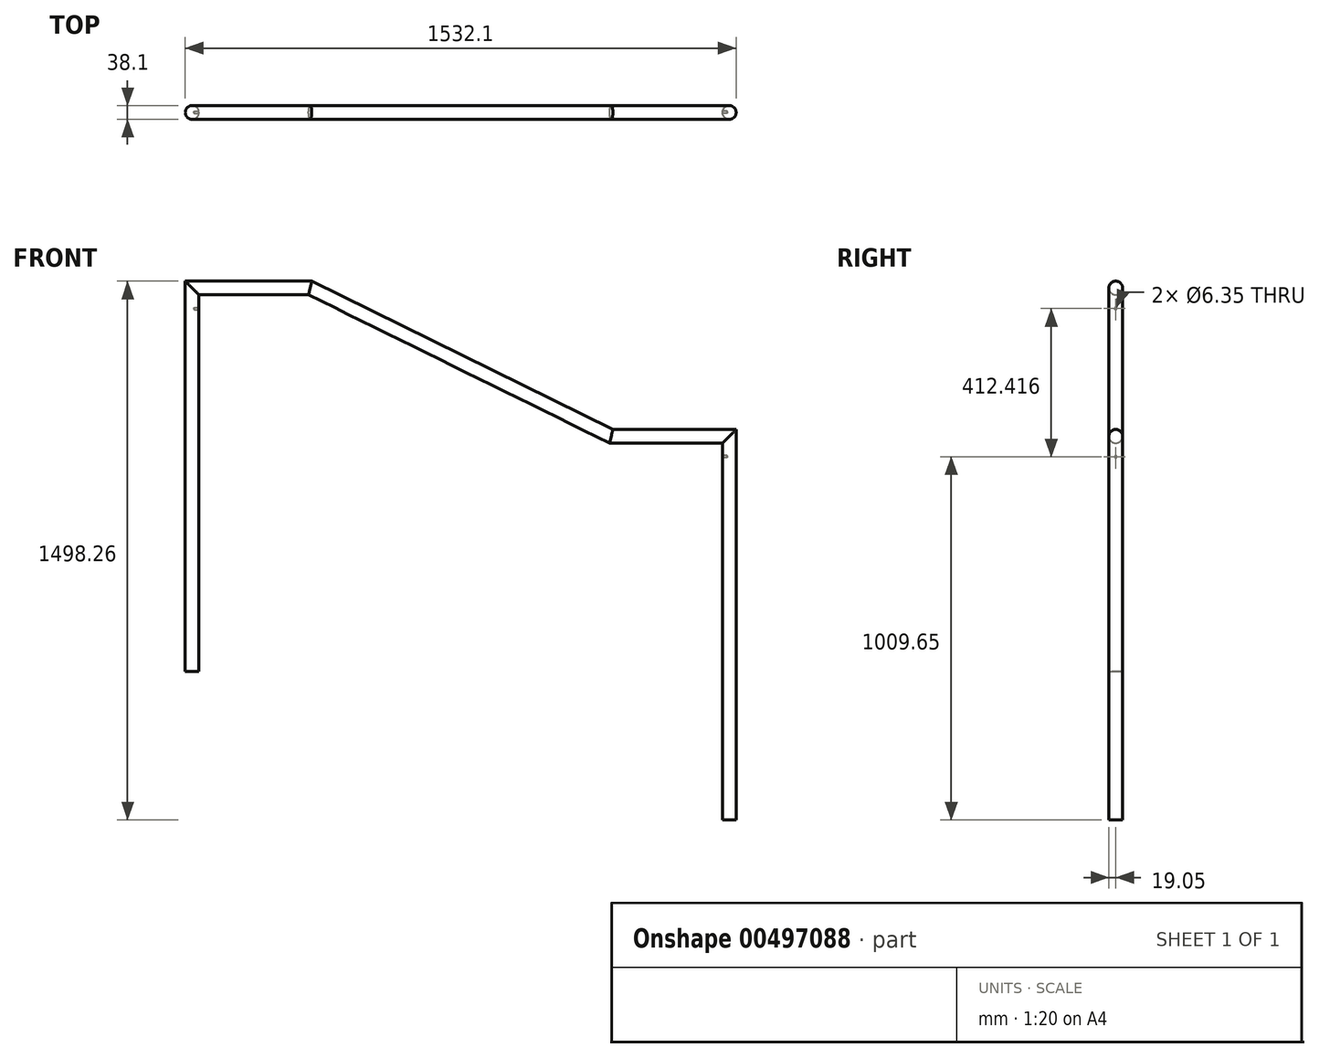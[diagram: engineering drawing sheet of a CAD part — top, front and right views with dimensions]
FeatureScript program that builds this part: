
annotation { "Feature Type Name" : "Feature", "Feature Type Description" : "" }
export const myFeature = defineFeature(function(context is Context, id is Id, definition is map)
    precondition{}
    {
        {
            var Q0;
            Q0=qCreatedBy(makeId("Front.planeOp"),FACE);
            var sketch = newSketch(context, id + "F0", { "sketchPlane" : qUnion([Q0])});
            skLineSegment(sketch, "E0", {"start": v(-626.32, -437.04) * mm, "end": v(-626.32, 629.76) * mm});
            skLineSegment(sketch, "E1", {"start": v(-626.32, 629.76) * mm, "end": v(-298.02, 629.76) * mm});
            skLineSegment(sketch, "E2", {"start": v(-298.02, 629.76) * mm, "end": v(539.38, 217.35) * mm});
            skLineSegment(sketch, "E3", {"start": v(539.38, 217.35) * mm, "end": v(867.68, 217.35) * mm});
            skLineSegment(sketch, "E4", {"start": v(867.68, 217.35) * mm, "end": v(867.68, -849.45) * mm});
            skLineSegment(sketch, "E5", {"start": v(539.38, 217.35) * mm, "end": v(124.02, 217.35) * mm, "construction": true});
            skSolve(sketch);
        }
        {
            var Q0;
            Q0=qCreatedBy(makeId("Top.planeOp"),FACE);
            var Q1;
            Q1=sQuery(id+"F0.wireOp",VERTEX,"E0.start");
            cPlane(context, id + "F1", {"entities" : qUnion([Q0, Q1]), "cplaneType" : CPlaneType.PLANE_POINT, "offset" : 25.4 * mm, "width" : 152.4 * mm, "height" : 152.4 * mm});
        }
        {
            var Q0;
            Q0=qCreatedBy(id+"F1.planeOp",FACE);
            var sketch = newSketch(context, id + "F2", { "sketchPlane" : qUnion([Q0])});
            skCircle(sketch, "E6", {"center": v(-626.32, 0) * mm, "radius": 19.05 * mm});
            skSolve(sketch);
        }
        {
            var Q0;
            Q0=makeQuery(id+"F2.imprint","IMPRINT",FACE,{"disambiguationData":[TD([[makeQuery(id+"F2.imprint","IMPRINT",EDGE,{"derivedFrom":sQuery(id+"F2.wireOp",EDGE,"E6")}),1.0]])]});
            var Q1;
            Q1=sQuery(id+"F0.wireOp",EDGE,"E0");
            var Q2;
            Q2=sQuery(id+"F0.wireOp",EDGE,"E1");
            var Q3;
            Q3=sQuery(id+"F0.wireOp",EDGE,"E2");
            var Q4;
            Q4=sQuery(id+"F0.wireOp",EDGE,"E3");
            var Q5;
            Q5=sQuery(id+"F0.wireOp",EDGE,"E4");
            sweep(context, id + "F3", {"profiles" : qUnion([Q0]), "path" : qUnion([Q1, Q2, Q3, Q4, Q5])});
        }
        {
            var Q0;
            Q0=makeQuery(id+"F3.opSweep","SWEPT_FACE",FACE,{"disambiguationData":[OSD([sQuery(id+"F0.wireOp",EDGE,"E0"),sQuery(id+"F2.wireOp",EDGE,"E6")])]});
            cPlane(context, id + "F4", {"entities" : qUnion([Q0]), "cplaneType" : CPlaneType.LINE_ANGLE, "offset" : 25.4 * mm, "angle" : 0 * degree, "width" : 152.4 * mm, "height" : 152.4 * mm});
        }
        {
            var Q0;
            Q0=makeQuery(id+"F3.opSweep","SWEPT_FACE",FACE,{"disambiguationData":[OSD([sQuery(id+"F0.wireOp",EDGE,"E0"),sQuery(id+"F2.wireOp",EDGE,"E6")])]});
            cPlane(context, id + "F5", {"entities" : qUnion([Q0]), "cplaneType" : CPlaneType.LINE_ANGLE, "offset" : 25.4 * mm, "angle" : 90 * degree, "width" : 152.4 * mm, "height" : 152.4 * mm});
        }
        {
            var Q0;
            Q0=qCreatedBy(id+"F5.planeOp",FACE);
            var sketch = newSketch(context, id + "F6", { "sketchPlane" : qUnion([Q0])});
            skLineSegment(sketch, "E7", {"start": v(607.27, 610.71) * mm, "end": v(607.27, 572.61) * mm, "construction": true});
            skSolve(sketch);
        }
        {
            var Q0;
            Q0=sQuery(id+"F6.wireOp",VERTEX,"E7.end");
            var Q1;
            Q1=qCreatedBy(id+"F4.planeOp",FACE);
            cPlane(context, id + "F7", {"entities" : qUnion([Q0, Q1]), "cplaneType" : CPlaneType.PLANE_POINT, "offset" : 25.4 * mm, "width" : 152.4 * mm, "height" : 152.4 * mm});
        }
        {
            var Q0;
            Q0=qCreatedBy(id+"F7.planeOp",FACE);
            var sketch = newSketch(context, id + "F8", { "sketchPlane" : qUnion([Q0])});
            skCircle(sketch, "E8", {"center": v(0, 572.61) * mm, "radius": 3.18 * mm, "construction": true});
            skSolve(sketch);
        }
        {
            var Q0;
            Q0=sQuery(id+"F8.wireOp",VERTEX,"E8.center");
            var Q1;
            Q1=makeQuery(id+"F3.opSweep","SWEPT_BODY",BODY,{"disambiguationData":[OSD([sQuery(id+"F0.wireOp",EDGE,"E4"),sQuery(id+"F2.wireOp",EDGE,"E6")])]});
            hole(context, id + "F9", {"style" : HoleStyle.SIMPLE, "endStyle" : HoleEndStyle.BLIND, "holeDiameter" : 6.35 * mm, "holeDepth" : 12.7 * mm, "isTappedThrough" : true, "tappedDepth" : 12.7 * mm, "tapClearance" : 3, "startFromSketch" : true, "locations" : qUnion([Q0]), "scope" : qUnion([Q1])});
        }
        {
            var Q0;
            Q0=makeQuery(id+"F3.opSweep","SWEPT_FACE",FACE,{"disambiguationData":[OSD([sQuery(id+"F0.wireOp",EDGE,"E4"),sQuery(id+"F2.wireOp",EDGE,"E6")])]});
            cPlane(context, id + "F10", {"entities" : qUnion([Q0]), "cplaneType" : CPlaneType.LINE_ANGLE, "offset" : 25.4 * mm, "angle" : 0 * degree, "width" : 152.4 * mm, "height" : 152.4 * mm});
        }
        {
            var Q0;
            Q0=makeQuery(id+"F3.opSweep","SWEPT_FACE",FACE,{"disambiguationData":[OSD([sQuery(id+"F0.wireOp",EDGE,"E4"),sQuery(id+"F2.wireOp",EDGE,"E6")])]});
            cPlane(context, id + "F11", {"entities" : qUnion([Q0]), "cplaneType" : CPlaneType.LINE_ANGLE, "offset" : 25.4 * mm, "angle" : 90 * degree, "width" : 152.4 * mm, "height" : 152.4 * mm});
        }
        {
            var Q0;
            Q0=qCreatedBy(id+"F11.planeOp",FACE);
            var sketch = newSketch(context, id + "F12", { "sketchPlane" : qUnion([Q0])});
            skLineSegment(sketch, "E9", {"start": v(-848.63, 198.3) * mm, "end": v(-848.63, 160.2) * mm, "construction": true});
            skSolve(sketch);
        }
        {
            var Q0;
            Q0=sQuery(id+"F12.wireOp",VERTEX,"E9.start");
            var Q1;
            Q1=qCreatedBy(id+"F10.planeOp",FACE);
            cPlane(context, id + "F13", {"entities" : qUnion([Q0, Q1]), "cplaneType" : CPlaneType.PLANE_POINT, "offset" : 25.4 * mm, "width" : 152.4 * mm, "height" : 152.4 * mm});
        }
        {
            var Q0;
            Q0=qCreatedBy(id+"F13.planeOp",FACE);
            var sketch = newSketch(context, id + "F14", { "sketchPlane" : qUnion([Q0])});
            skPoint(sketch, "E10", {"position": v(0, 160.2) * mm});
            skSolve(sketch);
        }
        {
            var Q0;
            Q0=sQuery(id+"F14.wireOp",VERTEX,"E10");
            var Q1;
            Q1=makeQuery(id+"F3.opSweep","SWEPT_BODY",BODY,{"disambiguationData":[OSD([sQuery(id+"F0.wireOp",EDGE,"E4"),sQuery(id+"F2.wireOp",EDGE,"E6")])]});
            hole(context, id + "F15", {"style" : HoleStyle.SIMPLE, "endStyle" : HoleEndStyle.BLIND, "holeDiameter" : 6.35 * mm, "holeDepth" : 12.7 * mm, "isTappedThrough" : true, "tappedDepth" : 12.7 * mm, "tapClearance" : 3, "startFromSketch" : true, "locations" : qUnion([Q0]), "scope" : qUnion([Q1])});
        }
    });
